# Revit family: Lav-Corian-North_America-Accessible-8254
name_source: partatom
category: Plumbing Fixtures
units: mm (PartAtom-declared; Revit-internal decimal feet)

## family parameters
Cut with Voids When Loaded = No
Host = Face
Maintain Annotation Orientation = No
OmniClass Number = 23.45.05.14.14
OmniClass Title = Sinks/Lavatories
Part Type = Normal
Room Calculation Point = No
Round Connector Dimension = Use Diameter
Shared = No

## types (1)
- 8254
    Assembly Code = D2010.7010
    CWFU = 0
    Cost = 0 $
    Default Elevation = 4' - 0"
    Depth = 0' - 6 3/4"
    Description = Lavatory North American Specification
    Finish = Solid Surface Sink - DuPont - Almond
    HWFU = 0
    Interior Length = 1' - 6"
    Interior Width = 1' - 0 3/4"
    Length = 1' - 7 1/2"
    Manufacturer = DuPont
    Model = 8254
    Product Page URL = http://www.dupont.com
    Sink Colors Available = Almond (Similar to Bone), Crema (Similar to Bisque), White Mocha (Similar to Cameo White), White Frost (Similar to Glacier White)
    URL = http://www.dupont.com
    Version = 2014 - v1.0a
    WFU = 1.75
    Width = 1' - 2 1/4"

## geometry (parser evidence)
native form markers: Sweep x1
no freeform markers — native parametric forms only
